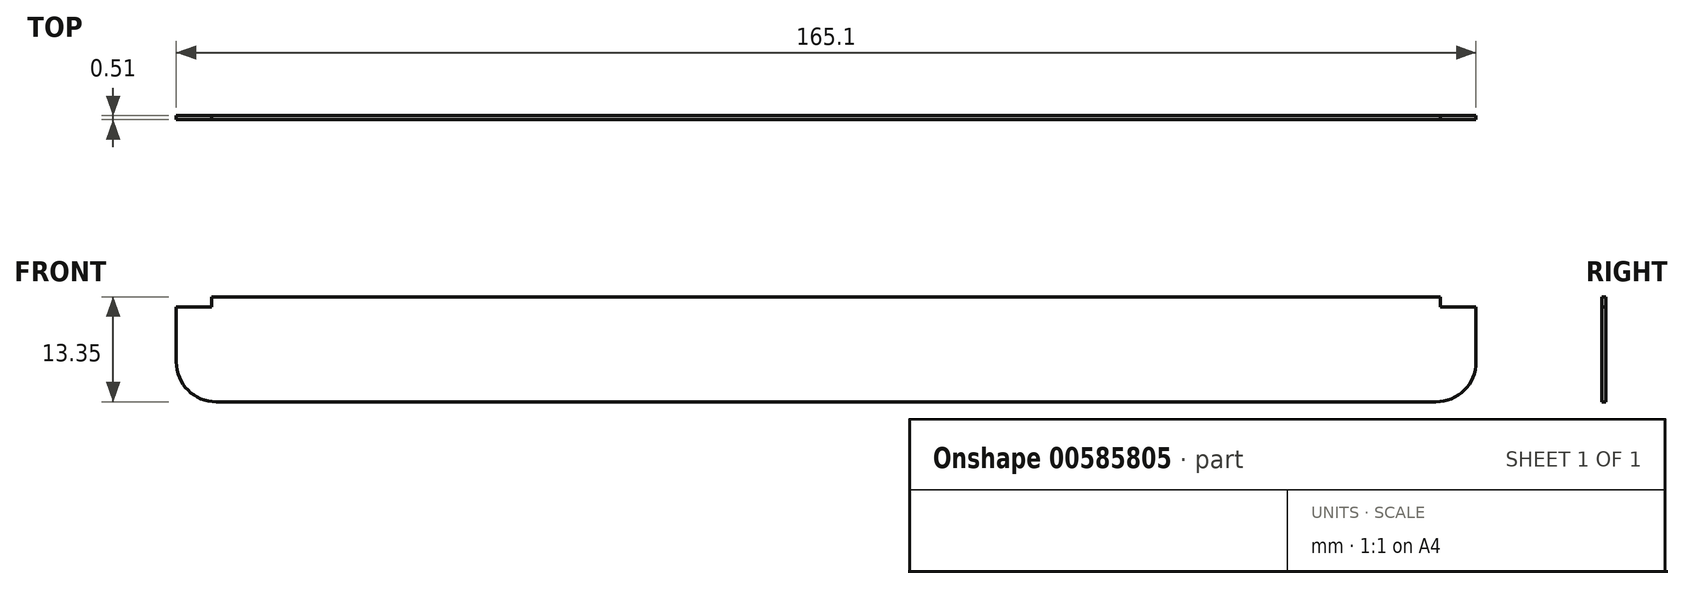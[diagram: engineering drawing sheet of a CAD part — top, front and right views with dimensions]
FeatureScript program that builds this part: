
annotation { "Feature Type Name" : "Feature", "Feature Type Description" : "" }
export const myFeature = defineFeature(function(context is Context, id is Id, definition is map)
    precondition{}
    {
        {
            var Q0;
            Q0=qCreatedBy(makeId("Front.planeOp"),FACE);
            var sketch = newSketch(context, id + "F0", { "sketchPlane" : qUnion([Q0])});
            skLineSegment(sketch, "E0.bottom", {"start": v(-70.52, 19.02) * mm, "end": v(-66.02, 19.02) * mm});
            skLineSegment(sketch, "E0.top", {"start": v(-65.44, 6.94) * mm, "end": v(89.5, 6.94) * mm});
            skLineSegment(sketch, "E0.left", {"start": v(-70.52, 19.02) * mm, "end": v(-70.52, 12.02) * mm});
            skLineSegment(sketch, "E0.right", {"start": v(94.58, 14.56) * mm, "end": v(94.58, 12.02) * mm});
            skPoint(sketch, "E1.middle", {"position": v(0, 16.8) * mm});
            skPoint(sketch, "E2.visualSharp", {"position": v(-70.52, 6.94) * mm});
            skArc(sketch, "E2.filletArc", {"start": v(-70.52, 12.02) * mm, "mid": v(-69.03, 8.42) * mm, "end": v(-65.44, 6.94) * mm});
            skPoint(sketch, "E3.visualSharp", {"position": v(94.58, 6.94) * mm});
            skArc(sketch, "E3.filletArc", {"start": v(89.5, 6.94) * mm, "mid": v(93.1, 8.42) * mm, "end": v(94.58, 12.02) * mm});
            skLineSegment(sketch, "E4.top", {"start": v(90.08, 20.3) * mm, "end": v(-66.02, 20.3) * mm});
            skLineSegment(sketch, "E4.left", {"start": v(90.08, 19.02) * mm, "end": v(90.08, 20.3) * mm});
            skLineSegment(sketch, "E4.right", {"start": v(-66.02, 19.02) * mm, "end": v(-66.02, 20.3) * mm});
            skPoint(sketch, "E4.middle", {"position": v(12.03, 16.8) * mm});
            skPoint(sketch, "E5.orphan", {"position": v(-66.02, 13.29) * mm});
            skPoint(sketch, "E6.orphan", {"position": v(90.08, 13.29) * mm});
            skLineSegment(sketch, "E7", {"start": v(90.08, 19.02) * mm, "end": v(94.58, 19.02) * mm});
            skLineSegment(sketch, "E8", {"start": v(94.58, 14.56) * mm, "end": v(94.58, 19.02) * mm});
            skSolve(sketch);
        }
        {
            var Q0;
            Q0=makeQuery(id+"F0.imprint","IMPRINT",FACE,{"disambiguationData":[TD([[makeQuery(id+"F0.imprint","IMPRINT",EDGE,{"derivedFrom":sQuery(id+"F0.wireOp",EDGE,"E0.bottom")}),-1.0]])]});
            extrude(context, id + "F1", {"entities" : qUnion([Q0]), "depth" : 0.5 * mm, "offsetDistance" : 25.4 * mm});
        }
    });
